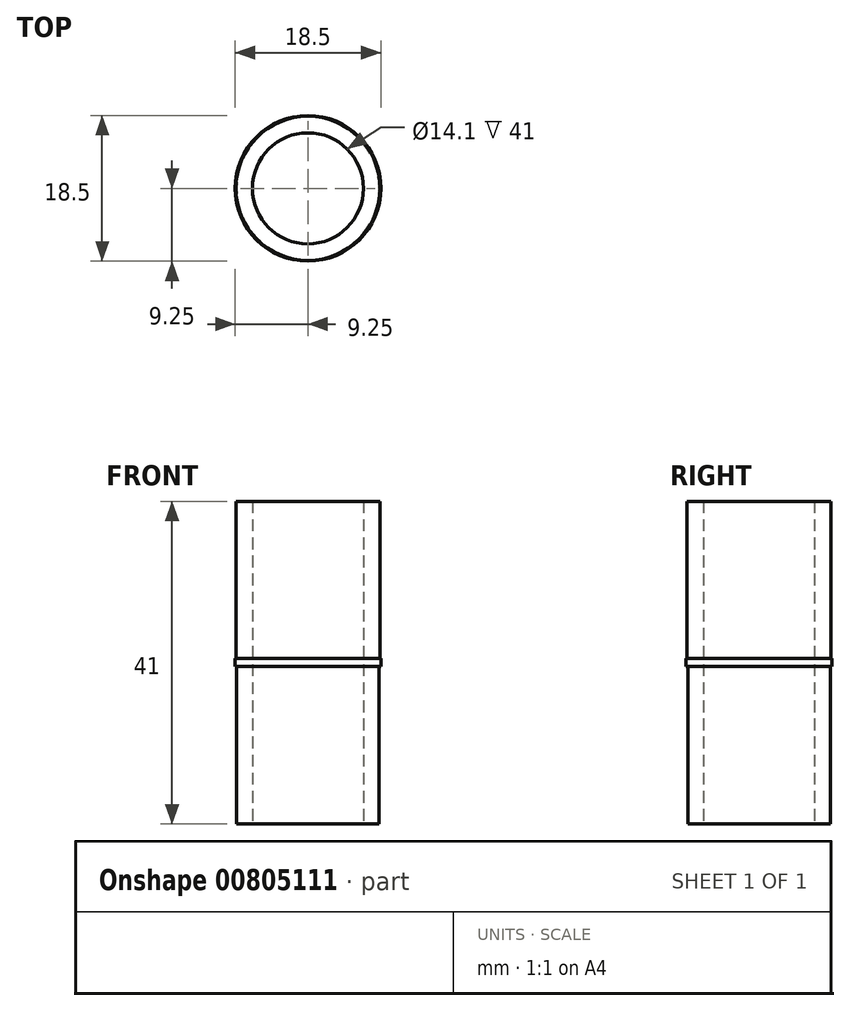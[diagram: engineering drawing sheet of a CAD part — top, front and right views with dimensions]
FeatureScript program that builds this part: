
annotation { "Feature Type Name" : "Feature", "Feature Type Description" : "" }
export const myFeature = defineFeature(function(context is Context, id is Id, definition is map)
    precondition{}
    {
        {
            var Q0;
            Q0=qCreatedBy(makeId("Top.planeOp"),FACE);
            var sketch = newSketch(context, id + "F0", { "sketchPlane" : qUnion([Q0])});
            skCircle(sketch, "E0", {"center": v(0, 0) * mm, "radius": 9.25 * mm});
            skSolve(sketch);
        }
        {
            var Q0;
            Q0=qSketchRegion(id+"F0",true);
            extrude(context, id + "F1", {"entities" : qUnion([Q0]), "depth" : 1 * mm, "offsetDistance" : 25 * mm});
        }
        {
            var Q0;
            Q0=makeQuery(id+"F1.opExtrude","CAP_FACE",FACE,{"disambiguationData":[OSD([sQuery(id+"F0.wireOp",EDGE,"E0")])],"isStart":false});
            var sketch = newSketch(context, id + "F2", { "sketchPlane" : qUnion([Q0])});
            skCircle(sketch, "E1", {"center": v(0, 0) * mm, "radius": 9.15 * mm});
            skSolve(sketch);
        }
        {
            var Q0;
            Q0=qSketchRegion(id+"F2",true);
            extrude(context, id + "F3", {"entities" : qUnion([Q0]), "operationType" : NewBodyOperationType.ADD, "depth" : 20 * mm, "offsetDistance" : 25 * mm});
        }
        {
            var Q0;
            Q0=makeQuery(id+"F1.opExtrude","CAP_FACE",FACE,{"disambiguationData":[OSD([sQuery(id+"F0.wireOp",EDGE,"E0")])],"isStart":true});
            var sketch = newSketch(context, id + "F4", { "sketchPlane" : qUnion([Q0])});
            skCircle(sketch, "E2", {"center": v(0, 0) * mm, "radius": 9.05 * mm});
            skSolve(sketch);
        }
        {
            var Q0;
            Q0 = qSketchRegion(id + "F4", true);
            extrude(context, id + "F5", {"entities" : qUnion([Q0]), "operationType" : NewBodyOperationType.ADD, "depth" : 20 * mm, "offsetDistance" : 25 * mm});
        }
        {
            var Q0;
            Q0=makeQuery(id+"F5.opExtrude","CAP_FACE",FACE,{"disambiguationData":[OSD([sQuery(id+"F4.wireOp",EDGE,"E2")])],"isStart":false});
            var sketch = newSketch(context, id + "F6", { "sketchPlane" : qUnion([Q0])});
            skCircle(sketch, "E3", {"center": v(0, 0) * mm, "radius": 7.05 * mm});
            skSolve(sketch);
        }
        {
            var Q0;
            Q0 = qSketchRegion(id + "F6", true);
            extrude(context, id + "F7", {"entities" : qUnion([Q0]), "operationType" : NewBodyOperationType.REMOVE, "endBound" : BoundingType.THROUGH_ALL, "oppositeDirection" : true, "depth" : 25 * mm, "offsetDistance" : 25 * mm});
        }
    });
